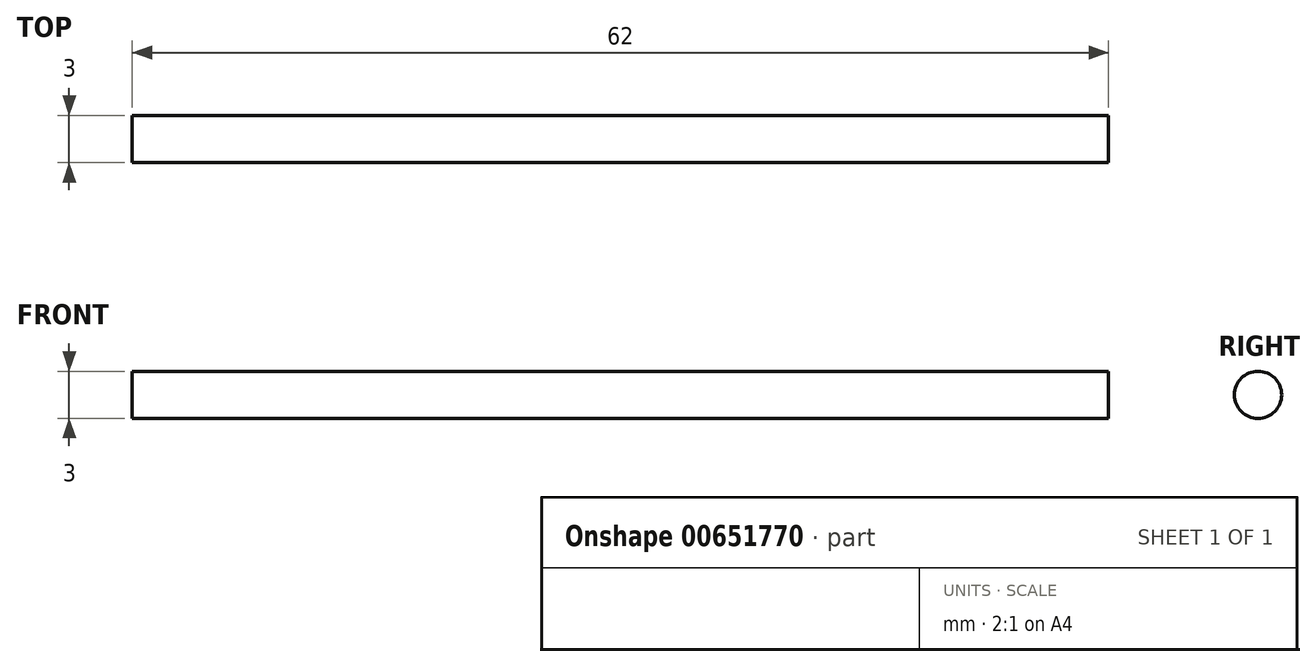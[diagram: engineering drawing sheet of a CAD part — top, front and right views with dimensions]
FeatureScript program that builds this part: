
annotation { "Feature Type Name" : "Feature", "Feature Type Description" : "" }
export const myFeature = defineFeature(function(context is Context, id is Id, definition is map)
    precondition{}
    {
        {
            var Q0;
            Q0=qCreatedBy(makeId("Right.planeOp"),FACE);
            var sketch = newSketch(context, id + "F0", { "sketchPlane" : qUnion([Q0])});
            skCircle(sketch, "E0", {"center": v(0, 6.92) * mm, "radius": 1.5 * mm});
            skSolve(sketch);
        }
        {
            var Q0;
            Q0=makeQuery(id+"F0.imprint","IMPRINT",FACE,{"disambiguationData":[TD([[makeQuery(id+"F0.imprint","IMPRINT",EDGE,{"derivedFrom":sQuery(id+"F0.wireOp",EDGE,"E0")}),1.0]])]});
            extrude(context, id + "F1", {"entities" : qUnion([Q0]), "endBound" : BoundingType.SYMMETRIC, "depth" : 62 * mm, "offsetDistance" : 25 * mm});
        }
    });
